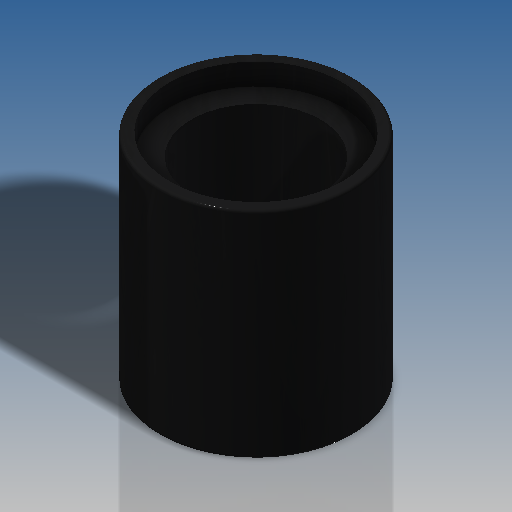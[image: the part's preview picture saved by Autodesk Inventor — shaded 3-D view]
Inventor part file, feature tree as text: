
AUTODESK INVENTOR PART (.ipt)
format: ipt  version: 2019.4 (Build 234330000, 330)  size: 186,880 bytes
history: native  units: in
note: dims shown in document units (in); Inventor stores cm internally (conversion verified against a paired STEP export)
features: revolve x1, fillet x1, sketch x1
ambient origin geometry x8: Origin, YZ Plane, XZ Plane, XY Plane, X Axis, Y Axis, Z Axis, Center Point
bodies: Solid1 (feature_tree)
feature tree (3):
  revolve  "Revolution1"  [1 undecoded]
  fillet  "Fillet1"  Radius=0.252in
  sketch  "Sketch1"  dims[d0=0.189in d1=0.315in d2=0.252in d3=0.0315in d4=0.2835in d5=90.0deg d6=0.0039in d7=0.0in d8=0.0in]
note: 1 required parameter value undecoded (feature->parameter linkage not recoverable at this tier; creation-order binding heuristic only, values carry confidence <= 0.55)
